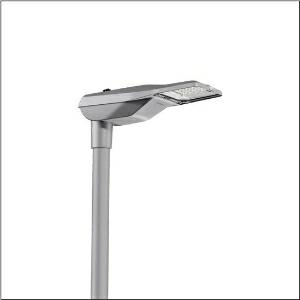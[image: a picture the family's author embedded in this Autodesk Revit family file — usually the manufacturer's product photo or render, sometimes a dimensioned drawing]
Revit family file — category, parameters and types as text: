
# Revit family: streetlight_sl_21_iq_micro___p0_8ab_5xe1r31v08cb_c843
name_source: partatom
category: Lighting Fixtures
units: mm (PartAtom-declared; Revit-internal decimal feet)

## family parameters
Cut with Voids When Loaded = No
Host = Face
Light Source = No
Part Type = Normal
Room Calculation Point = No
Round Connector Dimension = Use Diameter
Shared = No

## types (1)
- --- (1 x LED, 2570 lm, 19.1 W, 3000K)
    Apparent Load = 19 VA
    CIE Flux Codes = 36 71 98 100 100
    Color Rendering = 70
    Color Temperature = 3000K
    Default Elevation = 1800 mm
    Description = Streetlight SL 21 iQ micro, mast luminaire, primary light control with lens, of PMMA, primary optical cover: cover, of toughened safety glass, transparent, light distribution: P0.8aB, light emission: direct distribution, primary light characteristic: asymmetric, installation type: post-top, side-entry, LED, High Power LED, rated luminous flux: 2.570lm, luminous efficacy: 135lm/W, light colour: 730, colour temperature: 3000K, control gear: iQ-Street Remote, D4i with power reduction, control: pre-setting: logarithmic dimming characteristic, Street-Remote, Auto-Match, Temp-Guard, Lumen-Switch, Night-Set, Smart-Wire, Light-Fading, Desk-Remote (wireless, voltage-free reading and setting of iQ features in the workshop via application-optimized NFC function/RFID function), optimised constant luminous flux control (CLO 2.0), mains connection: 220..240V, AC, 50/60Hz, start of lifetime: 19W, end of service life: 20W, reduction: 9W, luminaire housing, of diecast aluminium, powder-coated, Siteco® metallic grey (DB 702S), corrosivity category C5 mid according to DIN EN ISO 12944, please order mast flange separately, inclination adjustable: 0°, 5°, 10°, 15°, sealing non-destructively replaceable, multi-level sealing system, length: 528mm, width: 235mm, height: 110mm, mast flange for spigot size: 42mm (side-entry): 5XC10008XM4, 60/48mm (side-entry/post-top): 5XC10108XM2, 76/60mm (side-entry/post-top): 5XC10108XM1, mounting height: 4..8m, Smart Interface above, protection rating (complete): IP66, insulation class (complete): insulation class II (safety insulation), certification: CE, ENEC, ENEC+, VDE, impact resistance: IK10, permissible operating ambient temperature for outdoor applications: -40..+50°C, standard-compliant lighting for roads and squares, packaging unit: 1 piece

Light Distribution: P0.8aB
    Height = 110 mm
    Lamp = 1 x LED
    Lamp Light Flux = 2570 lm
    Lamp Power = 19.1 W
    Lamp count = 1
    Length = 528 mm
    Luminous efficacy = 135 lm/W
    Manufacturer = Siteco
    ModVariant = No
    Model = 5XE1R31V08CB
    Number of Poles = 1
    OnlyDefault = Yes
    Power Factor = 1
    Product Name = Streetlight SL 21 iQ micro | P0.8aB
    Product group = mast luminaire | pylon top
    ProductGroupID = 6100
    Protection Class = Protection class II
    Protection Degree = IP 66
    RLX_Detail_Level = 1
    RLX_Emergency_Light_Flux = 0 lm
    RLX_Emergency_Type = 0
    RLX_Emergency_Type_DB = No
    RlxData = <blob elided: 98653 chars, md5=692781a3>
    Socket = socket
    Standby Power = 0 W
    System Light Flux = 2570 lm
    System Power = 19 W
    Type Comments = factory setting: luminous flux: 100 % | dim-lin: 254 | 387 mA
    Type Image = l_1277292.jpg
    URL = http://relux.com
    VarID = @adj_097181
    Voltage = 0 V
    Weight = 0.00 kg
    Width = 235 mm

## geometry (parser evidence)
native form markers: Blend x4, Sweep x9
no freeform markers — native parametric forms only
